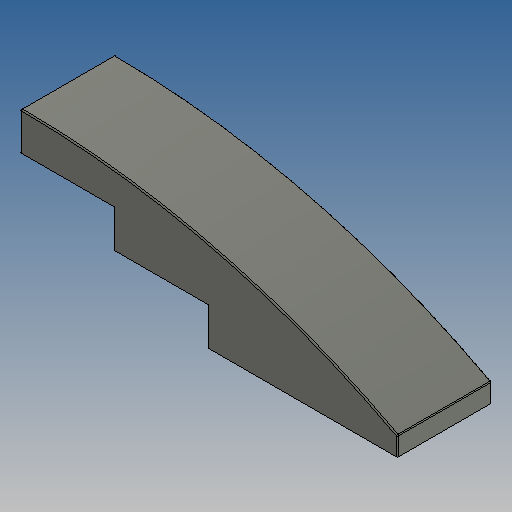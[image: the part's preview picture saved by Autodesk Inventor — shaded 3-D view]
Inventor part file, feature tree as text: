
AUTODESK INVENTOR PART (.ipt)
format: ipt  version: 2025 (Build 290162010, 162A)  size: 234,496 bytes
history: native  units: in
note: dims shown in document units (in); Inventor stores cm internally (conversion verified against a paired STEP export)
features: extrude x6, sketch x5, other x3, fillet x1
ambient origin geometry x8: Origin, YZ Plane, XZ Plane, XY Plane, X Axis, Y Axis, Z Axis, Center Point
bodies: Solid1 (feature_tree)
feature tree (15):
  extrude  "Extrusion1"  Depth=0.315in
  sketch  "Sketch10"  dims[d22=0.0039in d89=0.0in d90=0.0in]
  extrude  "Extrusion7"  Depth=0.378in TaperAngle=0.0deg
  extrude  "Extrusion8"  TaperAngle=0.0deg  [1 undecoded]
  extrude  "Extrusion2"  Depth=0.189in
  extrude  "Extrusion9"  Depth=0.063in
  extrude  "Extrusion10"  Depth=0.063in
  other  "Work Axis2"
  other  "Work Axis3"
  other  "Work Axis4"
  fillet  "Fillet1"  Radius=0.063in
  sketch  "Sketch2"  dims[d0=1.2598in d1=0.315in]
  sketch  "Sketch3"  dims[d4=0.378in d5=0.0in d7=0.0591in d11=0.3307in d12=0.0in]
  sketch  "Sketch11"  dims[d95=0.315in d96=0.0in d97=0.189in]
  sketch  "Sketch12"  dims[d98=0.0in d100=0.063in d102=0.063in d103=0.063in d104=0.063in d105=0.063in d107=0.063in d108=0.063in d109=0.189in d110=0.0in d112=0.0in d113=0.252in d114=0.126in d115=0.6299in d116=0.063in d118=0.0472in d119=0.0472in d120=0.3937in d121=0.0in d122=0.0472in d123=0.3937in d124=0.0in d125=0.0in d126=0.0in d127=0.0in d128=0.0in]
note: 1 required parameter value undecoded (feature->parameter linkage not recoverable at this tier; creation-order binding heuristic only, values carry confidence <= 0.55)
